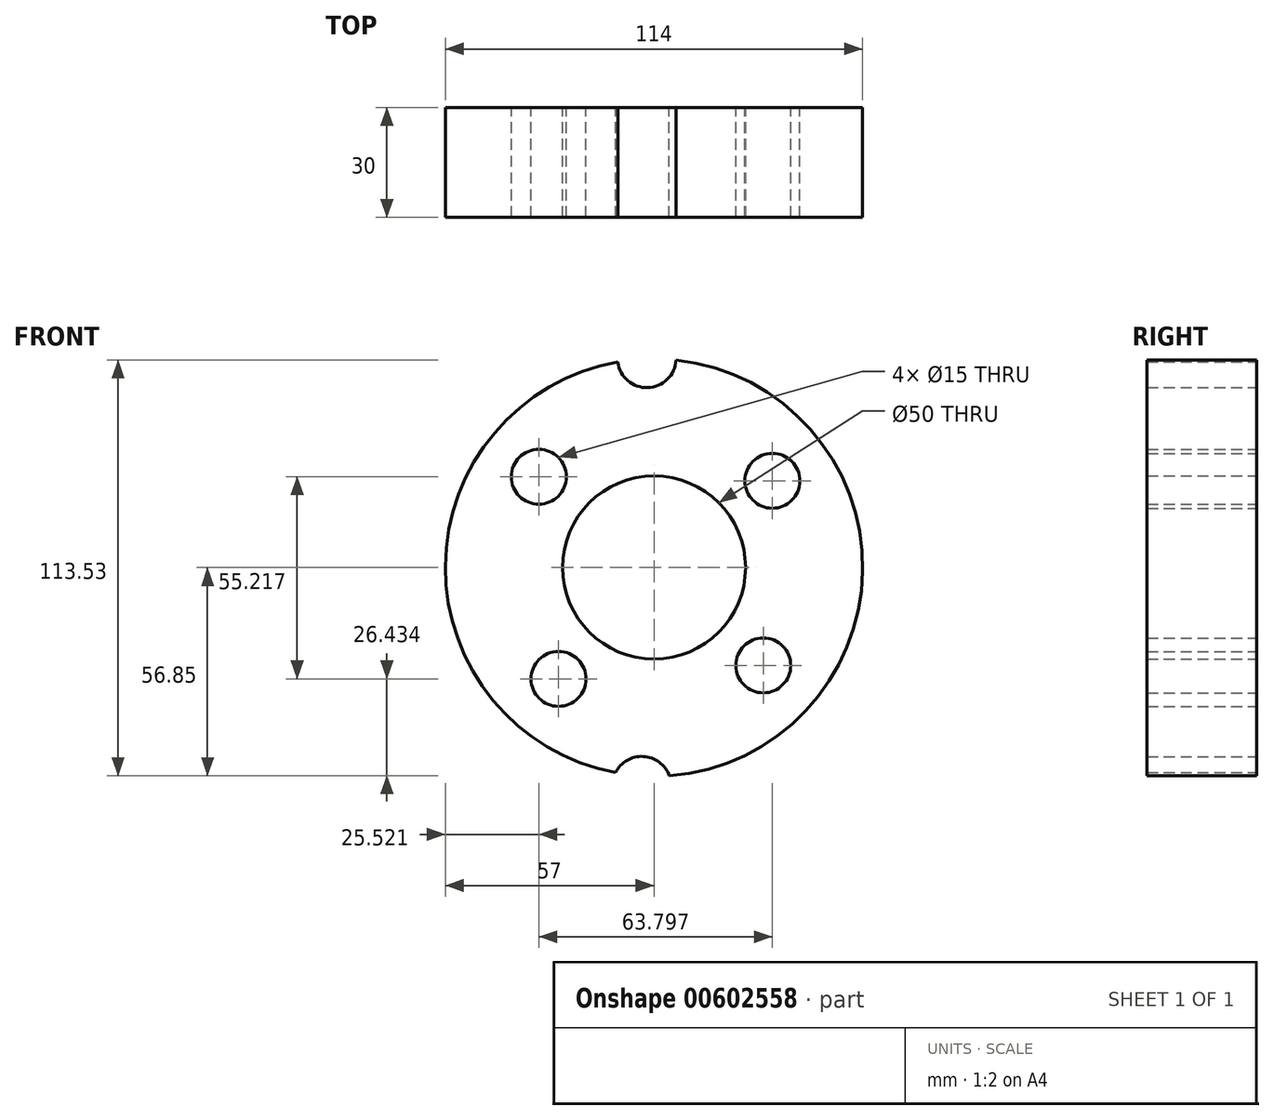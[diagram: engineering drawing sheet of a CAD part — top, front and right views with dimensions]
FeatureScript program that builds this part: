
annotation { "Feature Type Name" : "Feature", "Feature Type Description" : "" }
export const myFeature = defineFeature(function(context is Context, id is Id, definition is map)
    precondition{}
    {
        {
            var Q0;
            Q0=qCreatedBy(makeId("Front.planeOp"),FACE);
            var sketch = newSketch(context, id + "F0", { "sketchPlane" : qUnion([Q0])});
            skCircle(sketch, "E0", {"center": v(0, 0) * mm, "radius": 13 * mm});
            skCircle(sketch, "E1", {"center": v(0, 0) * mm, "radius": 25 * mm});
            skArc(sketch, "E2", {"start": v(-9.91, 56.13) * mm, "mid": v(-57, 0.3) * mm, "end": v(-10.51, -56.02) * mm});
            skArc(sketch, "E3", {"start": v(-35.55, 18.5) * mm, "mid": v(-39.89, -3.89) * mm, "end": v(-31.3, -25.02) * mm});
            skCircle(sketch, "E4", {"center": v(32.32, 23.7) * mm, "radius": 7.5 * mm});
            skCircle(sketch, "E5", {"center": v(-31.48, 24.8) * mm, "radius": 7.5 * mm});
            skCircle(sketch, "E6", {"center": v(-26.1, -30.42) * mm, "radius": 7.5 * mm});
            skCircle(sketch, "E7", {"center": v(29.86, -26.73) * mm, "radius": 7.5 * mm});
            skArc(sketch, "E8.trimOffspring", {"start": v(-19.97, -34.75) * mm, "mid": v(2.63, -39.99) * mm, "end": v(24.35, -31.83) * mm});
            skArc(sketch, "E9.trimOffspring", {"start": v(34.31, -20.7) * mm, "mid": v(40.03, -1.95) * mm, "end": v(36.17, 17.26) * mm});
            skArc(sketch, "E10.trimOffspring", {"start": v(27.34, 29.3) * mm, "mid": v(0.7, 40.07) * mm, "end": v(-26.3, 30.23) * mm});
            skArc(sketch, "E11", {"start": v(-9.91, 56.13) * mm, "mid": v(-1.7, 49.13) * mm, "end": v(6.01, 56.68) * mm});
            skArc(sketch, "E12", {"start": v(4.16, -56.85) * mm, "mid": v(-2.9, -51.6) * mm, "end": v(-10.51, -56.02) * mm});
            skArc(sketch, "E13.trimOffspring", {"start": v(4.16, -56.85) * mm, "mid": v(57, -0.93) * mm, "end": v(6.01, 56.68) * mm});
            skSolve(sketch);
        }
        {
            var Q0;
            Q0 = qSketchRegion(id + "F0", true);
            var Q1;
            Q1=makeQuery(id+"F0.imprint","IMPRINT",FACE,{"disambiguationData":[TD([[makeQuery(id+"F0.imprint","IMPRINT",EDGE,{"derivedFrom":sQuery(id+"F0.wireOp",EDGE,"E1")}),-1.0]])]});
            extrude(context, id + "F1", {"entities" : qUnion([Q0, Q1]), "depth" : 30 * mm, "offsetDistance" : 25 * mm});
        }
    });
